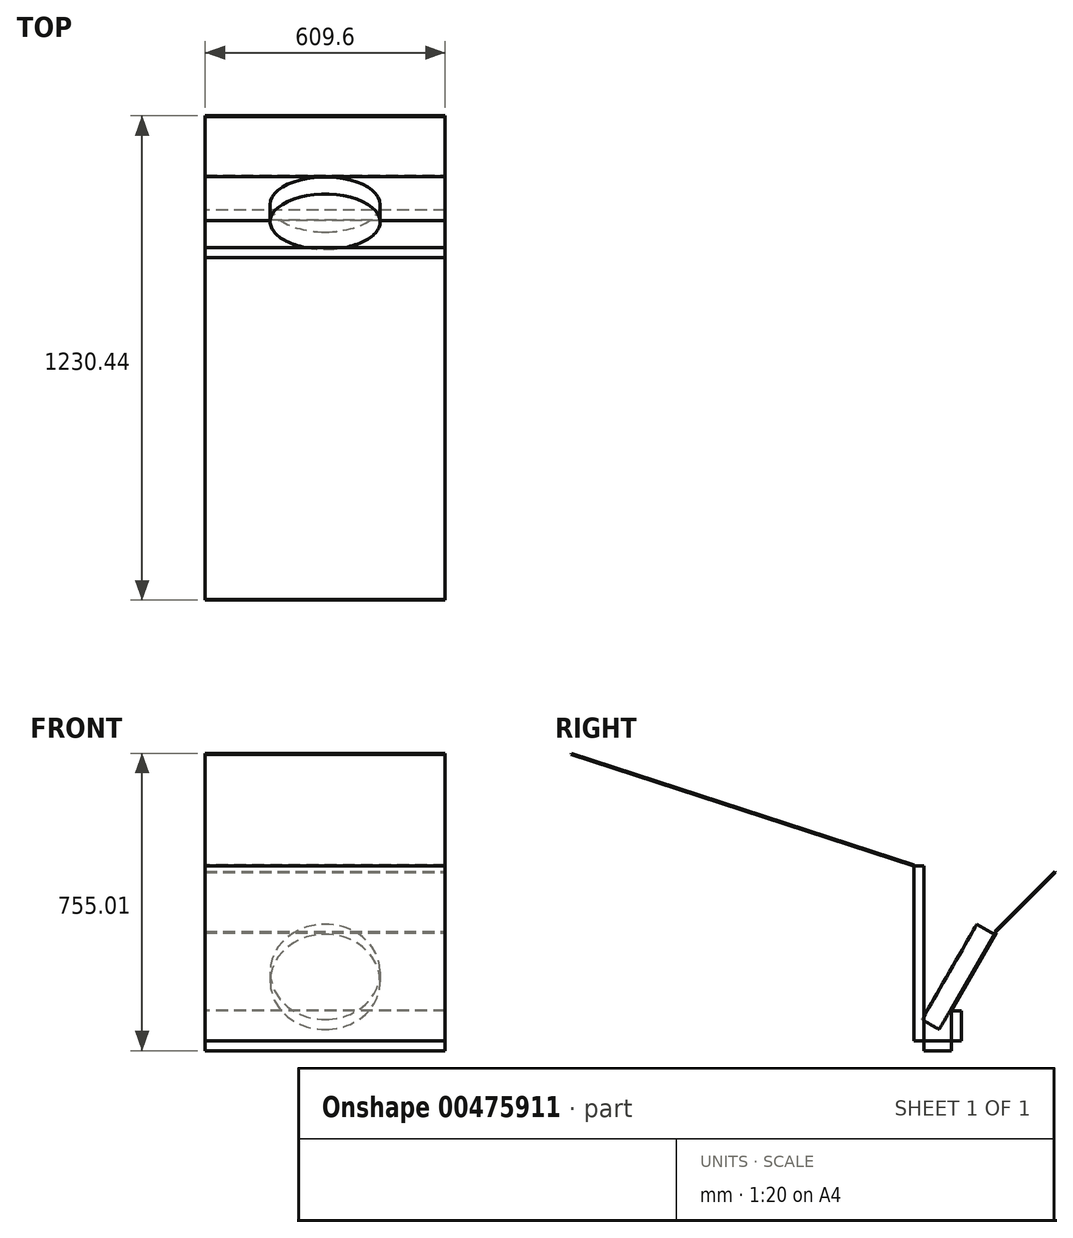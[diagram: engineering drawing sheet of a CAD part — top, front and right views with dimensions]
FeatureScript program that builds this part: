
annotation { "Feature Type Name" : "Feature", "Feature Type Description" : "" }
export const myFeature = defineFeature(function(context is Context, id is Id, definition is map)
    precondition{}
    {
        {
            var Q0;
            Q0=qCreatedBy(makeId("Front.planeOp"),FACE);
            var sketch = newSketch(context, id + "F0", { "sketchPlane" : qUnion([Q0])});
            skLineSegment(sketch, "E0.bottom", {"start": v(304.8, 232) * mm, "end": v(-304.8, 232) * mm});
            skLineSegment(sketch, "E0.top", {"start": v(304.8, -212.5) * mm, "end": v(-304.8, -212.5) * mm});
            skLineSegment(sketch, "E0.left", {"start": v(304.8, 232) * mm, "end": v(304.8, -212.5) * mm});
            skLineSegment(sketch, "E0.right", {"start": v(-304.8, 232) * mm, "end": v(-304.8, -212.5) * mm});
            skPoint(sketch, "E0.middle", {"position": v(0, 9.75) * mm});
            skSolve(sketch);
        }
        {
            var Q0;
            Q0=qSketchRegion(id+"F0",true);
            extrude(context, id + "F1", {"entities" : qUnion([Q0]), "depth" : 25.4 * mm, "offsetDistance" : 25.4 * mm});
        }
        {
            var Q0;
            Q0=makeQuery(id+"F1.opExtrude","SWEPT_FACE",FACE,{"disambiguationData":[OSD([sQuery(id+"F0.wireOp",EDGE,"E0.top")])]});
            var sketch = newSketch(context, id + "F2", { "sketchPlane" : qUnion([Q0])});
            skLineSegment(sketch, "E1.bottom", {"start": v(-304.8, 0) * mm, "end": v(304.8, 0) * mm});
            skLineSegment(sketch, "E1.top", {"start": v(-304.8, -69.85) * mm, "end": v(304.8, -69.85) * mm});
            skLineSegment(sketch, "E1.left", {"start": v(-304.8, 0) * mm, "end": v(-304.8, -69.85) * mm});
            skLineSegment(sketch, "E1.right", {"start": v(304.8, 0) * mm, "end": v(304.8, -69.85) * mm});
            skSolve(sketch);
        }
        {
            var Q0;
            Q0=qSketchRegion(id+"F2",true);
            extrude(context, id + "F3", {"entities" : qUnion([Q0]), "depth" : 25.4 * mm, "offsetDistance" : 25.4 * mm});
        }
        {
            var Q0;
            Q0=makeQuery(id+"F3.opExtrude","SWEPT_FACE",FACE,{"disambiguationData":[OSD([sQuery(id+"F2.wireOp",EDGE,"E1.top")])]});
            var sketch = newSketch(context, id + "F4", { "sketchPlane" : qUnion([Q0])});
            skLineSegment(sketch, "E2.bottom", {"start": v(-304.8, -136.3) * mm, "end": v(304.8, -136.3) * mm});
            skLineSegment(sketch, "E2.top", {"start": v(-304.8, -212.5) * mm, "end": v(304.8, -212.5) * mm});
            skLineSegment(sketch, "E2.left", {"start": v(-304.8, -136.3) * mm, "end": v(-304.8, -212.5) * mm});
            skLineSegment(sketch, "E2.right", {"start": v(304.8, -136.3) * mm, "end": v(304.8, -212.5) * mm});
            skSolve(sketch);
        }
        {
            var Q0;
            Q0=qSketchRegion(id+"F4",true);
            extrude(context, id + "F5", {"entities" : qUnion([Q0]), "depth" : 25.4 * mm, "offsetDistance" : 25.4 * mm});
        }
        {
            var Q0;
            Q0=makeQuery(id+"F5.opExtrude","CAP_FACE",FACE,{"disambiguationData":[OSD([sQuery(id+"F4.wireOp",EDGE,"E2.bottom"),sQuery(id+"F4.wireOp",EDGE,"E2.top"),sQuery(id+"F4.wireOp",EDGE,"E2.left"),sQuery(id+"F4.wireOp",EDGE,"E2.right")])],"isStart":true});
            var sketch = newSketch(context, id + "F6", { "sketchPlane" : qUnion([Q0])});
            skLineSegment(sketch, "E3.bottom", {"start": v(-304.8, -136.3) * mm, "end": v(304.8, -136.3) * mm});
            skLineSegment(sketch, "E3.top", {"start": v(-304.8, 92.3) * mm, "end": v(304.8, 92.3) * mm});
            skLineSegment(sketch, "E3.left", {"start": v(-304.8, -136.3) * mm, "end": v(-304.8, 92.3) * mm});
            skLineSegment(sketch, "E3.right", {"start": v(304.8, -136.3) * mm, "end": v(304.8, 92.3) * mm});
            skSolve(sketch);
        }
        {
            var Q0;
            Q0=qSketchRegion(id+"F6",true);
            extrude(context, id + "F7", {"entities" : qUnion([Q0]), "depth" : 2.54 * mm, "offsetDistance" : 25.4 * mm});
        }
        {
            var Q0;
            Q0=makeQuery(id+"F7.opExtrude","SWEPT_BODY",BODY,{"disambiguationData":[OSD([sQuery(id+"F6.wireOp",EDGE,"E3.bottom"),sQuery(id+"F6.wireOp",EDGE,"E3.top"),sQuery(id+"F6.wireOp",EDGE,"E3.left"),sQuery(id+"F6.wireOp",EDGE,"E3.right")])]});
            var Q1;
            Q1=makeQuery(id+"F5.opExtrude","CAP_EDGE",EDGE,{"disambiguationData":[OSD([sQuery(id+"F4.wireOp",EDGE,"E2.bottom")])],"isStart":true});
            transform(context, id + "F8", {"entities" : qUnion([Q0]), "transformType" : TransformType.ROTATION, "transformAxis" : qUnion([Q1]), "angle" : 30 * degree, "makeCopy" : false});
        }
        {
            var Q0;
            Q0=makeQuery(id+"F7.opExtrude","CAP_FACE",FACE,{"disambiguationData":[OSD([sQuery(id+"F6.wireOp",EDGE,"E3.bottom"),sQuery(id+"F6.wireOp",EDGE,"E3.top"),sQuery(id+"F6.wireOp",EDGE,"E3.left"),sQuery(id+"F6.wireOp",EDGE,"E3.right")])],"isStart":false});
            var sketch = newSketch(context, id + "F9", { "sketchPlane" : qUnion([Q0])});
            skLineSegment(sketch, "E4.bottom", {"start": v(-304.8, 361.39) * mm, "end": v(304.8, 361.39) * mm});
            skLineSegment(sketch, "E4.top", {"start": v(-304.8, 145.49) * mm, "end": v(304.8, 145.49) * mm});
            skLineSegment(sketch, "E4.left", {"start": v(-304.8, 145.49) * mm, "end": v(-304.8, 361.39) * mm});
            skLineSegment(sketch, "E4.right", {"start": v(304.8, 145.49) * mm, "end": v(304.8, 361.39) * mm});
            skSolve(sketch);
        }
        {
            var Q0;
            Q0=makeQuery(id+"F9.imprint","IMPRINT",FACE,{"disambiguationData":[TD([[makeQuery(id+"F9.imprint","IMPRINT",EDGE,{"derivedFrom":sQuery(id+"F9.wireOp",EDGE,"E4.bottom")}),-1.0]])]});
            extrude(context, id + "F10", {"entities" : qUnion([Q0]), "depth" : 2.54 * mm, "offsetDistance" : 25.4 * mm});
        }
        {
            var Q0;
            Q0=makeQuery(id+"F10.opExtrude","SWEPT_BODY",BODY,{"disambiguationData":[OSD([sQuery(id+"F9.wireOp",EDGE,"E4.bottom"),sQuery(id+"F9.wireOp",EDGE,"E4.top"),sQuery(id+"F9.wireOp",EDGE,"E4.left"),sQuery(id+"F9.wireOp",EDGE,"E4.right")])]});
            var Q1;
            Q1=makeQuery(id+"F7.opExtrude","CAP_EDGE",EDGE,{"disambiguationData":[OSD([sQuery(id+"F6.wireOp",EDGE,"E3.top")])],"isStart":false});
            transform(context, id + "F11", {"entities" : qUnion([Q0]), "transformType" : TransformType.ROTATION, "transformAxis" : qUnion([Q1]), "angle" : 15 * degree, "oppositeDirection" : true, "makeCopy" : false});
        }
        {
            var Q0;
            Q0=makeQuery(id+"F7.opExtrude","CAP_FACE",FACE,{"disambiguationData":[OSD([sQuery(id+"F6.wireOp",EDGE,"E3.bottom"),sQuery(id+"F6.wireOp",EDGE,"E3.top"),sQuery(id+"F6.wireOp",EDGE,"E3.left"),sQuery(id+"F6.wireOp",EDGE,"E3.right")])],"isStart":false});
            var sketch = newSketch(context, id + "F12", { "sketchPlane" : qUnion([Q0])});
            skCircle(sketch, "E5", {"center": v(0, 0) * mm, "radius": 139.7 * mm});
            skPoint(sketch, "E6", {"position": v(0, 145.49) * mm});
            skLineSegment(sketch, "E7", {"start": v(0, 145.49) * mm, "end": v(0, -83.11) * mm});
            skSolve(sketch);
        }
        {
            var Q0;
            Q0=qSketchRegion(id+"F12",true);
            extrude(context, id + "F13", {"entities" : qUnion([Q0]), "depth" : 50.8 * mm, "offsetDistance" : 25.4 * mm});
        }
        {
            var Q0;
            Q0=makeQuery(id+"F1.opExtrude","SWEPT_FACE",FACE,{"disambiguationData":[OSD([sQuery(id+"F0.wireOp",EDGE,"E0.bottom")])]});
            var sketch = newSketch(context, id + "F14", { "sketchPlane" : qUnion([Q0])});
            skLineSegment(sketch, "E8.bottom", {"start": v(-304.8, -939.8) * mm, "end": v(304.8, -939.8) * mm});
            skLineSegment(sketch, "E8.top", {"start": v(-304.8, -25.4) * mm, "end": v(304.8, -25.4) * mm});
            skLineSegment(sketch, "E8.left", {"start": v(-304.8, -939.8) * mm, "end": v(-304.8, -25.4) * mm});
            skLineSegment(sketch, "E8.right", {"start": v(304.8, -939.8) * mm, "end": v(304.8, -25.4) * mm});
            skSolve(sketch);
        }
        {
            var Q0;
            Q0=qSketchRegion(id+"F14",true);
            extrude(context, id + "F15", {"entities" : qUnion([Q0]), "depth" : 2.54 * mm, "offsetDistance" : 25.4 * mm});
        }
        {
            var Q0;
            Q0=makeQuery(id+"F15.opExtrude","SWEPT_BODY",BODY,{"disambiguationData":[OSD([sQuery(id+"F14.wireOp",EDGE,"E8.bottom"),sQuery(id+"F14.wireOp",EDGE,"E8.top"),sQuery(id+"F14.wireOp",EDGE,"E8.left"),sQuery(id+"F14.wireOp",EDGE,"E8.right")])]});
            var Q1;
            Q1=makeQuery(id+"F15.opExtrude","CAP_EDGE",EDGE,{"disambiguationData":[OSD([sQuery(id+"F14.wireOp",EDGE,"E8.top")])],"isStart":false});
            transform(context, id + "F16", {"entities" : qUnion([Q0]), "transformType" : TransformType.ROTATION, "transformAxis" : qUnion([Q1]), "angle" : 18 * degree, "makeCopy" : false});
        }
    });
